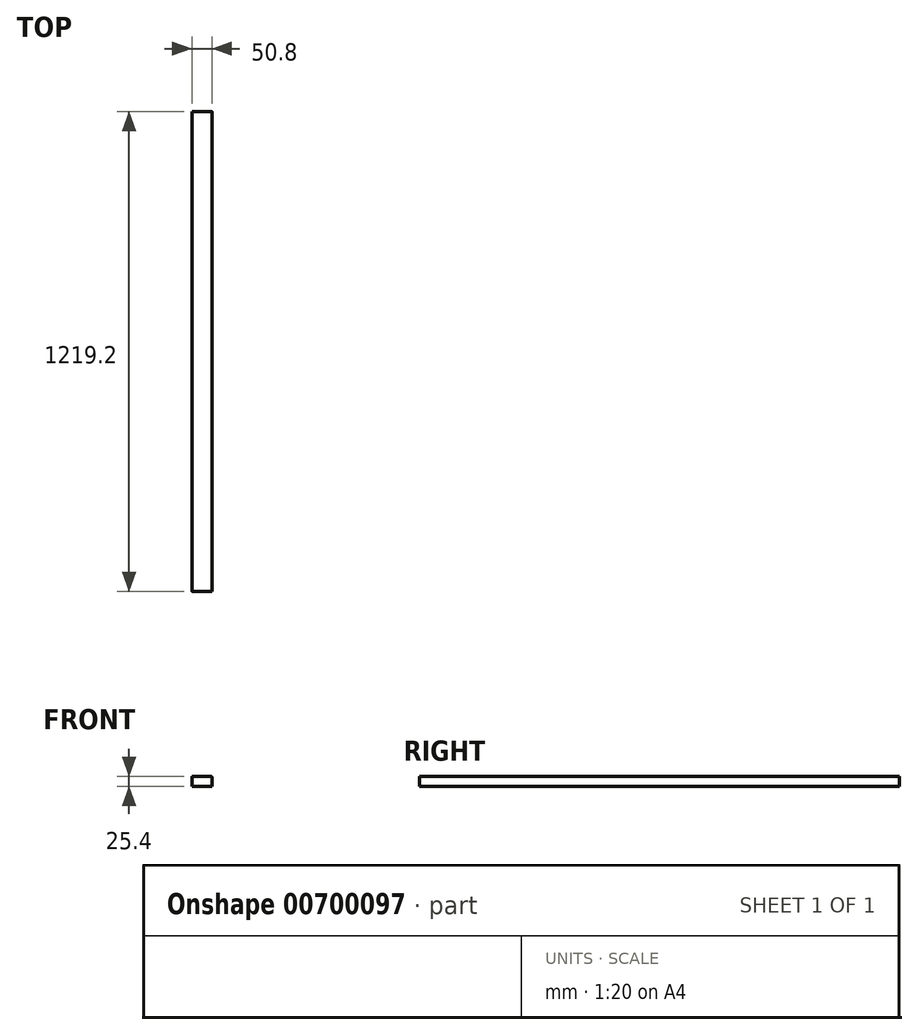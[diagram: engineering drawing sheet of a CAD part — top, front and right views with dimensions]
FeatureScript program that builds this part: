
annotation { "Feature Type Name" : "Feature", "Feature Type Description" : "" }
export const myFeature = defineFeature(function(context is Context, id is Id, definition is map)
    precondition{}
    {
        {
            var Q0;
            Q0=qCreatedBy(makeId("Front.planeOp"),FACE);
            var sketch = newSketch(context, id + "F0", { "sketchPlane" : qUnion([Q0])});
            skLineSegment(sketch, "E0.bottom", {"start": v(-25.4, -25.4) * mm, "end": v(25.4, -25.4) * mm});
            skLineSegment(sketch, "E0.top", {"start": v(-25.4, 25.4) * mm, "end": v(25.4, 25.4) * mm});
            skLineSegment(sketch, "E0.left", {"start": v(-25.4, -25.4) * mm, "end": v(-25.4, 25.4) * mm});
            skLineSegment(sketch, "E0.right", {"start": v(25.4, -25.4) * mm, "end": v(25.4, 25.4) * mm});
            skPoint(sketch, "E0.middle", {"position": v(0, 0) * mm});
            skSolve(sketch);
        }
        {
            var Q0;
            Q0=makeQuery(id+"F0.imprint","IMPRINT",FACE,{"disambiguationData":[TD([[makeQuery(id+"F0.imprint","IMPRINT",EDGE,{"derivedFrom":sQuery(id+"F0.wireOp",EDGE,"E0.bottom")}),1.0]])]});
            extrude(context, id + "F1", {"entities" : qUnion([Q0]), "endBound" : BoundingType.SYMMETRIC, "depth" : 609.6 * mm, "offsetDistance" : 25.4 * mm});
        }
        {
            var Q0;
            Q0=makeQuery(id+"F1.opExtrude","SWEPT_FACE",FACE,{"disambiguationData":[OSD([sQuery(id+"F0.wireOp",EDGE,"E0.top")])]});
            extrude(context, id + "F2", {"entities" : qUnion([Q0]), "operationType" : NewBodyOperationType.REMOVE, "oppositeDirection" : true, "depth" : 12.7 * mm, "offsetDistance" : 25.4 * mm});
        }
        {
            var Q0;
            Q0=makeQuery(id+"F1.opExtrude","SWEPT_FACE",FACE,{"disambiguationData":[OSD([sQuery(id+"F0.wireOp",EDGE,"E0.bottom")])]});
            extrude(context, id + "F3", {"entities" : qUnion([Q0]), "operationType" : NewBodyOperationType.REMOVE, "oppositeDirection" : true, "depth" : 12.7 * mm, "offsetDistance" : 25.4 * mm});
        }
        {
            var Q0;
            Q0=makeQuery(id+"F1.opExtrude","CAP_FACE",FACE,{"disambiguationData":[OSD([sQuery(id+"F0.wireOp",EDGE,"E0.bottom"),sQuery(id+"F0.wireOp",EDGE,"E0.top"),sQuery(id+"F0.wireOp",EDGE,"E0.left"),sQuery(id+"F0.wireOp",EDGE,"E0.right")])],"isStart":true});
            extrude(context, id + "F4", {"entities" : qUnion([Q0]), "operationType" : NewBodyOperationType.ADD, "depth" : 304.8 * mm, "offsetDistance" : 25.4 * mm});
        }
        {
            var Q0;
            Q0=makeQuery(id+"F1.opExtrude","CAP_FACE",FACE,{"disambiguationData":[OSD([sQuery(id+"F0.wireOp",EDGE,"E0.bottom"),sQuery(id+"F0.wireOp",EDGE,"E0.top"),sQuery(id+"F0.wireOp",EDGE,"E0.left"),sQuery(id+"F0.wireOp",EDGE,"E0.right")])],"isStart":false});
            extrude(context, id + "F5", {"entities" : qUnion([Q0]), "operationType" : NewBodyOperationType.ADD, "depth" : 304.8 * mm, "offsetDistance" : 25.4 * mm});
        }
        {
            var Q0;
            {var subQ0=sQuery(id+"F0.wireOp",EDGE,"E0.left");var subQ1=sQuery(id+"F0.wireOp",EDGE,"E0.top");Q0=makeQuery(id+"F5.boolean.opBoolean","MERGE",EDGE,{"derivedFrom":[makeQuery(id+"F4.boolean.opBoolean","MERGE",EDGE,{"derivedFrom":[makeQuery(id+"F2.boolean.opBoolean","COPY",EDGE,{"derivedFrom":makeQuery(id+"F2.opExtrude","CAP_EDGE",EDGE,{"disambiguationData":[OSD([subQ1,subQ0])],"isStart":false})}),makeQuery(id+"F4.opExtrude","SWEPT_EDGE",EDGE,{"disambiguationData":[OSD([subQ1,subQ0])]})]}),makeQuery(id+"F5.opExtrude","SWEPT_EDGE",EDGE,{"disambiguationData":[OSD([subQ1,subQ0])]})]});}
            var Q1;
            {var subQ0=sQuery(id+"F0.wireOp",EDGE,"E0.right");var subQ1=sQuery(id+"F0.wireOp",EDGE,"E0.top");Q1=makeQuery(id+"F5.boolean.opBoolean","MERGE",EDGE,{"derivedFrom":[makeQuery(id+"F4.boolean.opBoolean","MERGE",EDGE,{"derivedFrom":[makeQuery(id+"F2.boolean.opBoolean","COPY",EDGE,{"derivedFrom":makeQuery(id+"F2.opExtrude","CAP_EDGE",EDGE,{"disambiguationData":[OSD([subQ1,subQ0])],"isStart":false})}),makeQuery(id+"F4.opExtrude","SWEPT_EDGE",EDGE,{"disambiguationData":[OSD([subQ1,subQ0])]})]}),makeQuery(id+"F5.opExtrude","SWEPT_EDGE",EDGE,{"disambiguationData":[OSD([subQ1,subQ0])]})]});}
            fillet(context, id + "F6", {"entities" : qUnion([Q0, Q1]), "radius" : 2.54 * mm, "tangentPropagation" : true, "allowEdgeOverflow" : false});
        }
    });
